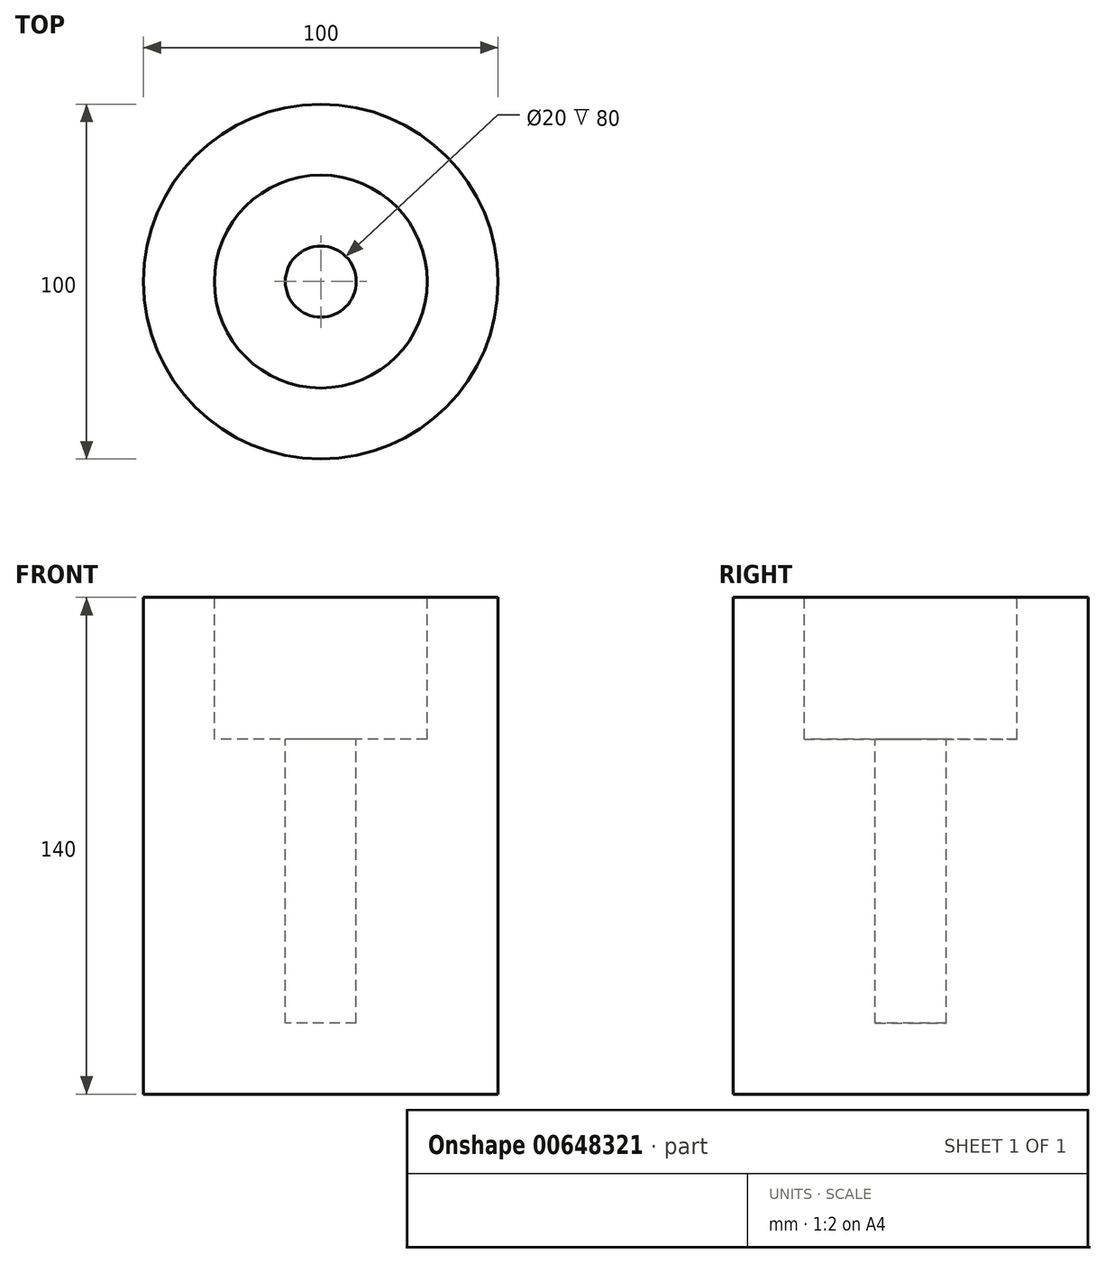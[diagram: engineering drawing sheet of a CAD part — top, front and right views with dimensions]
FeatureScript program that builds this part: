
annotation { "Feature Type Name" : "Feature", "Feature Type Description" : "" }
export const myFeature = defineFeature(function(context is Context, id is Id, definition is map)
    precondition{}
    {
        {
            var Q0;
            Q0=qCreatedBy(makeId("Top.planeOp"),FACE);
            var sketch = newSketch(context, id + "F0", { "sketchPlane" : qUnion([Q0])});
            skCircle(sketch, "E0", {"center": v(0, 0) * mm, "radius": 50 * mm});
            skSolve(sketch);
        }
        {
            var Q0;
            Q0=makeQuery(id+"F0.imprint","IMPRINT",FACE,{"disambiguationData":[TD([[makeQuery(id+"F0.imprint","IMPRINT",EDGE,{"derivedFrom":sQuery(id+"F0.wireOp",EDGE,"E0")}),1.0]])]});
            extrude(context, id + "F1", {"entities" : qUnion([Q0]), "endBound" : BoundingType.SYMMETRIC, "depth" : 140 * mm, "offsetDistance" : 25 * mm});
        }
        {
            var Q0;
            Q0=makeQuery(id+"F1.opExtrude","CAP_FACE",FACE,{"disambiguationData":[OSD([sQuery(id+"F0.wireOp",EDGE,"E0")])],"isStart":false});
            var sketch = newSketch(context, id + "F2", { "sketchPlane" : qUnion([Q0])});
            skCircle(sketch, "E1", {"center": v(0, 0) * mm, "radius": 10 * mm});
            skCircle(sketch, "E2", {"center": v(0, 0) * mm, "radius": 30 * mm});
            skSolve(sketch);
        }
        {
            var Q0;
            Q0=makeQuery(id+"F2.imprint","IMPRINT",FACE,{"disambiguationData":[TD([[makeQuery(id+"F2.imprint","IMPRINT",EDGE,{"derivedFrom":sQuery(id+"F2.wireOp",EDGE,"E1")}),1.0]])]});
            extrude(context, id + "F3", {"entities" : qUnion([Q0]), "operationType" : NewBodyOperationType.REMOVE, "oppositeDirection" : true, "depth" : 120 * mm, "offsetDistance" : 25 * mm});
        }
        {
            var Q0;
            Q0=makeQuery(id+"F2.imprint","IMPRINT",FACE,{"disambiguationData":[TD([[makeQuery(id+"F2.imprint","IMPRINT",EDGE,{"derivedFrom":sQuery(id+"F2.wireOp",EDGE,"E1")}),-1.0]])]});
            extrude(context, id + "F4", {"entities" : qUnion([Q0]), "operationType" : NewBodyOperationType.REMOVE, "oppositeDirection" : true, "depth" : 40 * mm, "offsetDistance" : 25 * mm});
        }
    });
